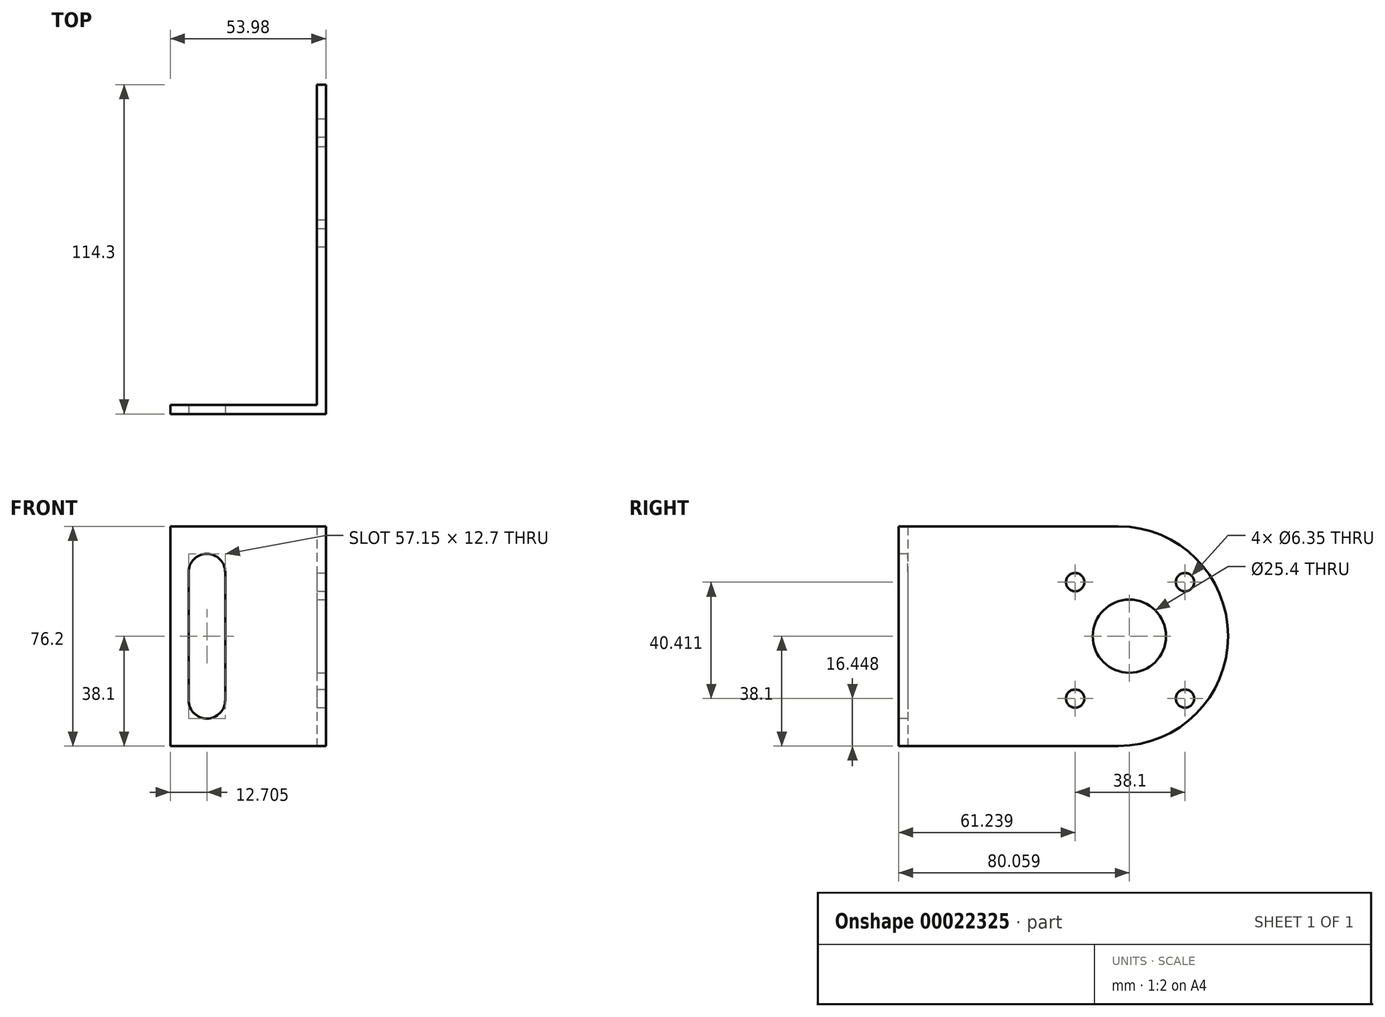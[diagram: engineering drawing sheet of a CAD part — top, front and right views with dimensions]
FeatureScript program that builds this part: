
annotation { "Feature Type Name" : "Feature", "Feature Type Description" : "" }
export const myFeature = defineFeature(function(context is Context, id is Id, definition is map)
    precondition{}
    {
        {
            var Q0;
            Q0=qCreatedBy(makeId("Top.planeOp"),FACE);
            var sketch = newSketch(context, id + "F0", { "sketchPlane" : qUnion([Q0])});
            skLineSegment(sketch, "E0", {"start": v(0, 0) * mm, "end": v(0, -117.48) * mm});
            skLineSegment(sketch, "E1", {"start": v(0, -117.48) * mm, "end": v(-53.98, -117.48) * mm});
            skLineSegment(sketch, "E2", {"start": v(-53.98, -117.48) * mm, "end": v(-53.98, -114.3) * mm});
            skLineSegment(sketch, "E3", {"start": v(-53.98, -114.3) * mm, "end": v(-3.17, -114.3) * mm});
            skLineSegment(sketch, "E4", {"start": v(-3.17, -114.3) * mm, "end": v(-3.18, 0) * mm});
            skLineSegment(sketch, "E5", {"start": v(-3.18, 0) * mm, "end": v(-3.18, 0) * mm});
            skLineSegment(sketch, "E6", {"start": v(-3.18, 0) * mm, "end": v(0, 0) * mm});
            skSolve(sketch);
        }
        {
            var Q0;
            Q0=makeQuery(id+"F0.imprint","IMPRINT",FACE,{"disambiguationData":[TD([[makeQuery(id+"F0.imprint","IMPRINT",EDGE,{"derivedFrom":sQuery(id+"F0.wireOp",EDGE,"E0")}),-1.0]])]});
            extrude(context, id + "F1", {"entities" : qUnion([Q0]), "depth" : 76.2 * mm});
        }
        {
            var Q0;
            Q0=makeQuery(id+"F1.opExtrude","SWEPT_FACE",FACE,{"disambiguationData":[OSD([sQuery(id+"F0.wireOp",EDGE,"E4")])]});
            var sketch = newSketch(context, id + "F2", { "sketchPlane" : qUnion([Q0])});
            skLineSegment(sketch, "E7", {"start": v(114.3, 39.73) * mm, "end": v(41.28, 39.73) * mm});
            skCircle(sketch, "E8", {"center": v(41.28, 39.73) * mm, "radius": 12.7 * mm});
            skArc(sketch, "E9", {"start": v(41.28, 76.2) * mm, "mid": v(3.18, 38.1) * mm, "end": v(41.27, 0) * mm});
            skSolve(sketch);
        }
        {
            var Q0;
            {var subQ2=sQuery(id+"F2.wireOp",EDGE,"E9");Q0=makeQuery(id+"F2.imprint","IMPRINT",FACE,{"disambiguationData":[TD([[makeQuery(id+"F2.imprint","IMPRINT",EDGE,{"derivedFrom":subQ2}),-1.0]])]});}
            extrude(context, id + "F3", {"entities" : qUnion([Q0]), "operationType" : NewBodyOperationType.REMOVE, "endBound" : BoundingType.UP_TO_NEXT, "oppositeDirection" : true, "depth" : 25.4 * mm});
        }
        {
            var Q0;
            Q0=qCreatedBy(makeId("Right.planeOp"),FACE);
            var sketch = newSketch(context, id + "F4", { "sketchPlane" : qUnion([Q0])});
            skLineSegment(sketch, "E10", {"start": v(-37.41, 76.2) * mm, "end": v(-37.41, 0) * mm});
            skCircle(sketch, "E11", {"center": v(-37.41, 38.1) * mm, "radius": 12.7 * mm});
            skSolve(sketch);
        }
        {
            var Q0;
            {var subQ0=sQuery(id+"F4.wireOp",EDGE,"E11");var subQ1=sQuery(id+"F4.wireOp",EDGE,"E10");var subQ3=makeQuery(id+"F4.imprint","INTERSECT",VERTEX,{"disambiguationData":[OD(0.0)],"derivedFrom":[subQ1,subQ0]});Q0=makeQuery(id+"F4.imprint","IMPRINT",FACE,{"disambiguationData":[TD([[makeQuery(id+"F4.imprint","IMPRINT",EDGE,{"disambiguationData":[TD([[subQ3,1.0]])],"derivedFrom":subQ1}),1.0]])]});}
            var Q1;
            {var subQ0=sQuery(id+"F4.wireOp",EDGE,"E11");var subQ1=sQuery(id+"F4.wireOp",EDGE,"E10");var subQ3=makeQuery(id+"F4.imprint","INTERSECT",VERTEX,{"disambiguationData":[OD(0.0)],"derivedFrom":[subQ1,subQ0]});Q1=makeQuery(id+"F4.imprint","IMPRINT",FACE,{"disambiguationData":[TD([[makeQuery(id+"F4.imprint","IMPRINT",EDGE,{"disambiguationData":[TD([[subQ3,1.0]])],"derivedFrom":subQ1}),-1.0]])]});}
            var Q2;
            Q2 = qSketchRegion(id + "F6", true);
            extrude(context, id + "F5", {"entities" : qUnion([Q0, Q1, Q2]), "operationType" : NewBodyOperationType.REMOVE, "endBound" : BoundingType.UP_TO_NEXT, "oppositeDirection" : true, "depth" : 25.4 * mm});
        }
        {
            var Q0;
            Q0=qCreatedBy(makeId("Right.planeOp"),FACE);
            var sketch = newSketch(context, id + "F6", { "sketchPlane" : qUnion([Q0])});
            skLineSegment(sketch, "E12", {"start": v(-37.18, 36.65) * mm, "end": v(-37.18, 56.86) * mm});
            skLineSegment(sketch, "E13", {"start": v(-37.18, 56.86) * mm, "end": v(-56.23, 56.86) * mm});
            skLineSegment(sketch, "E14", {"start": v(-37.18, 56.86) * mm, "end": v(-18.13, 56.86) * mm});
            skCircle(sketch, "E15", {"center": v(-18.13, 56.86) * mm, "radius": 3.18 * mm});
            skCircle(sketch, "E16", {"center": v(-56.23, 56.86) * mm, "radius": 3.18 * mm});
            skLineSegment(sketch, "E17", {"start": v(-37.18, 36.65) * mm, "end": v(-37.18, 16.45) * mm});
            skLineSegment(sketch, "E18", {"start": v(-37.18, 16.45) * mm, "end": v(-18.13, 16.45) * mm});
            skLineSegment(sketch, "E19", {"start": v(-37.18, 16.45) * mm, "end": v(-56.23, 16.45) * mm});
            skCircle(sketch, "E20", {"center": v(-56.23, 16.45) * mm, "radius": 3.18 * mm});
            skCircle(sketch, "E21", {"center": v(-18.13, 16.45) * mm, "radius": 3.18 * mm});
            skSolve(sketch);
        }
        {
            var Q0;
            Q0=makeQuery(id+"F1.opExtrude","SWEPT_FACE",FACE,{"disambiguationData":[OSD([sQuery(id+"F0.wireOp",EDGE,"E1")])]});
            var sketch = newSketch(context, id + "F7", { "sketchPlane" : qUnion([Q0])});
            skLineSegment(sketch, "E22", {"start": v(-53.98, 38.1) * mm, "end": v(-34.93, 38.1) * mm});
            skLineSegment(sketch, "E23", {"start": v(-34.93, 38.1) * mm, "end": v(-34.93, 15.88) * mm});
            skLineSegment(sketch, "E24", {"start": v(-34.93, 38.1) * mm, "end": v(-34.93, 60.33) * mm});
            skLineSegment(sketch, "E25", {"start": v(-34.93, 15.88) * mm, "end": v(-47.62, 15.88) * mm});
            skLineSegment(sketch, "E26.bottom", {"start": v(-34.93, 60.33) * mm, "end": v(-47.62, 60.33) * mm});
            skLineSegment(sketch, "E26.left", {"start": v(-34.93, 60.33) * mm, "end": v(-34.93, 15.88) * mm});
            skLineSegment(sketch, "E26.right", {"start": v(-47.62, 60.33) * mm, "end": v(-47.62, 15.88) * mm});
            skArc(sketch, "E27", {"start": v(-34.93, 60.33) * mm, "mid": v(-41.28, 66.68) * mm, "end": v(-47.62, 60.33) * mm});
            skArc(sketch, "E28", {"start": v(-47.62, 15.88) * mm, "mid": v(-41.28, 9.53) * mm, "end": v(-34.93, 15.88) * mm});
            skSolve(sketch);
        }
        {
            var Q0;
            {var subQ3=sQuery(id+"F7.wireOp",EDGE,"E25");Q0=makeQuery(id+"F7.imprint","IMPRINT",FACE,{"disambiguationData":[TD([[makeQuery(id+"F7.imprint","IMPRINT",EDGE,{"derivedFrom":subQ3}),-1.0]])]});}
            var Q1;
            {var subQ3=sQuery(id+"F7.wireOp",EDGE,"E26.bottom");Q1=makeQuery(id+"F7.imprint","IMPRINT",FACE,{"disambiguationData":[TD([[makeQuery(id+"F7.imprint","IMPRINT",EDGE,{"derivedFrom":subQ3}),1.0]])]});}
            var Q2;
            Q2=makeQuery(id+"F7.imprint","IMPRINT",FACE,{"disambiguationData":[TD([[makeQuery(id+"F7.imprint","IMPRINT",EDGE,{"derivedFrom":sQuery(id+"F7.wireOp",EDGE,"E26.bottom")}),-1.0]])]});
            var Q3;
            Q3=makeQuery(id+"F7.imprint","IMPRINT",FACE,{"disambiguationData":[TD([[makeQuery(id+"F7.imprint","IMPRINT",EDGE,{"derivedFrom":sQuery(id+"F7.wireOp",EDGE,"E25")}),1.0]])]});
            extrude(context, id + "F8", {"entities" : qUnion([Q0, Q1, Q2, Q3]), "operationType" : NewBodyOperationType.REMOVE, "endBound" : BoundingType.UP_TO_NEXT, "oppositeDirection" : true, "depth" : 25.4 * mm});
        }
        {
            var Q0;
            Q0=makeQuery(id+"F6.imprint","IMPRINT",FACE,{"disambiguationData":[TD([[makeQuery(id+"F6.imprint","IMPRINT",EDGE,{"derivedFrom":sQuery(id+"F6.wireOp",EDGE,"E16")}),1.0]])]});
            var Q1;
            Q1=makeQuery(id+"F6.imprint","IMPRINT",FACE,{"disambiguationData":[TD([[makeQuery(id+"F6.imprint","IMPRINT",EDGE,{"derivedFrom":sQuery(id+"F6.wireOp",EDGE,"E15")}),1.0]])]});
            var Q2;
            Q2=makeQuery(id+"F6.imprint","IMPRINT",FACE,{"disambiguationData":[TD([[makeQuery(id+"F6.imprint","IMPRINT",EDGE,{"derivedFrom":sQuery(id+"F6.wireOp",EDGE,"E20")}),1.0]])]});
            var Q3;
            Q3=makeQuery(id+"F6.imprint","IMPRINT",FACE,{"disambiguationData":[TD([[makeQuery(id+"F6.imprint","IMPRINT",EDGE,{"derivedFrom":sQuery(id+"F6.wireOp",EDGE,"E21")}),1.0]])]});
            extrude(context, id + "F9", {"entities" : qUnion([Q0, Q1, Q2, Q3]), "operationType" : NewBodyOperationType.REMOVE, "endBound" : BoundingType.UP_TO_NEXT, "oppositeDirection" : true, "depth" : 25.4 * mm});
        }
    });
